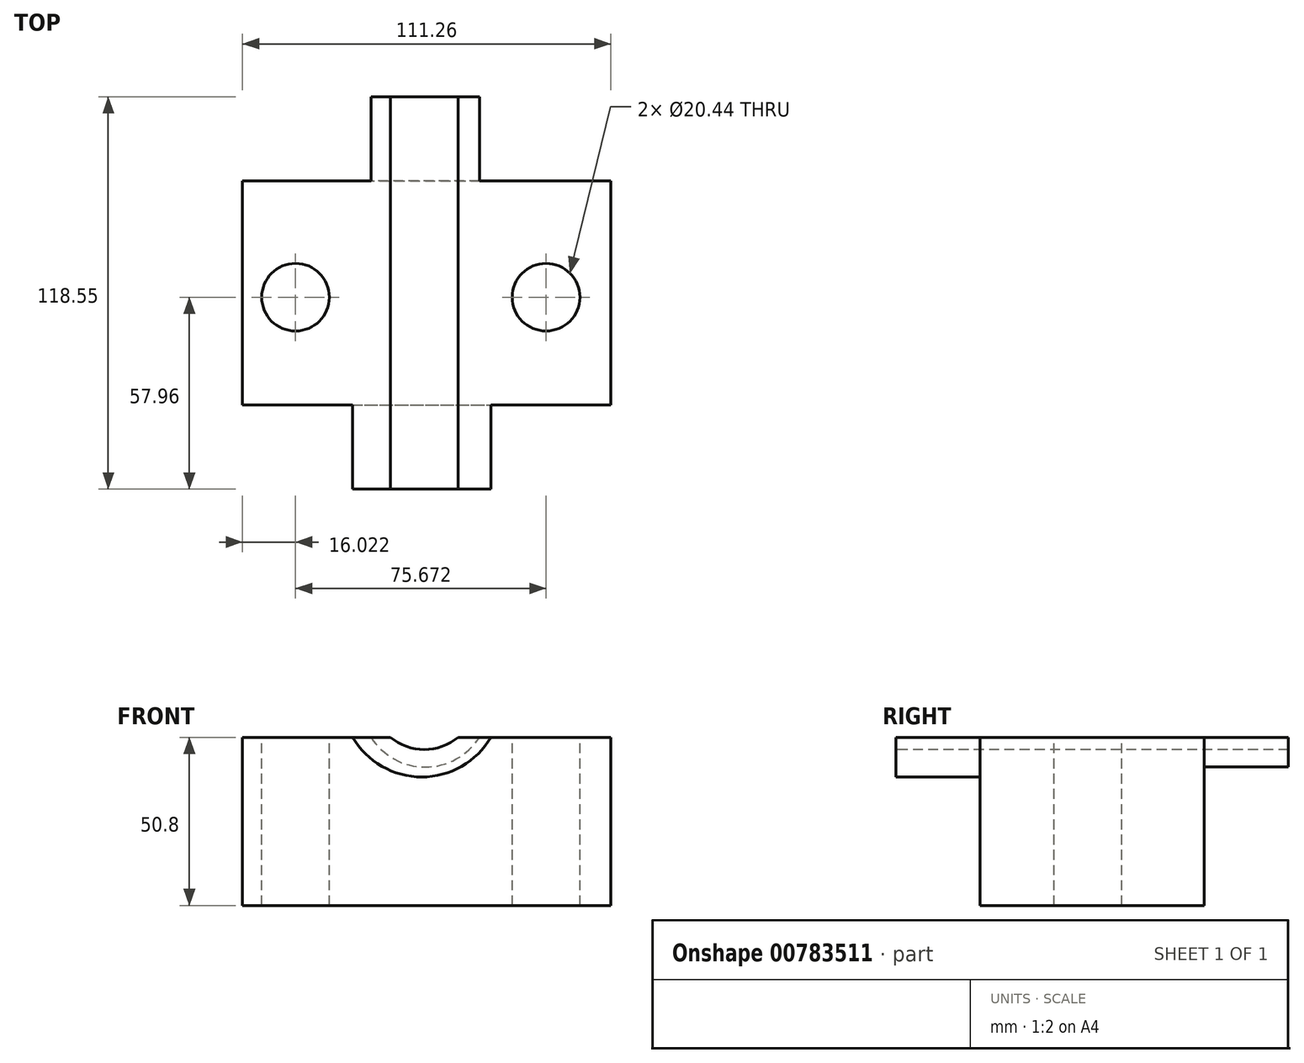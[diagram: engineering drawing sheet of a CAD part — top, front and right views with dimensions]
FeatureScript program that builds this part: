
annotation { "Feature Type Name" : "Feature", "Feature Type Description" : "" }
export const myFeature = defineFeature(function(context is Context, id is Id, definition is map)
    precondition{}
    {
        {
            var Q0;
            Q0=qCreatedBy(makeId("Top.planeOp"),FACE);
            var sketch = newSketch(context, id + "F0", { "sketchPlane" : qUnion([Q0])});
            skLineSegment(sketch, "E0.bottom", {"start": v(-54.46, -32.56) * mm, "end": v(56.8, -32.56) * mm});
            skLineSegment(sketch, "E0.top", {"start": v(-54.46, 35.19) * mm, "end": v(56.8, 35.19) * mm});
            skLineSegment(sketch, "E0.left", {"start": v(-54.46, -32.56) * mm, "end": v(-54.46, 35.19) * mm});
            skLineSegment(sketch, "E0.right", {"start": v(56.8, -32.56) * mm, "end": v(56.8, 35.19) * mm});
            skSolve(sketch);
        }
        {
            var Q0;
            Q0=makeQuery(id+"F0.imprint","IMPRINT",FACE,{"disambiguationData":[TD([[makeQuery(id+"F0.imprint","IMPRINT",EDGE,{"derivedFrom":sQuery(id+"F0.wireOp",EDGE,"E0.bottom")}),1.0]])]});
            extrude(context, id + "F1", {"entities" : qUnion([Q0]), "depth" : 50.8 * mm, "offsetDistance" : 25.4 * mm});
        }
        {
            var Q0;
            Q0=makeQuery(id+"F1.opExtrude","SWEPT_FACE",FACE,{"disambiguationData":[OSD([sQuery(id+"F0.wireOp",EDGE,"E0.bottom")])]});
            var sketch = newSketch(context, id + "F2", { "sketchPlane" : qUnion([Q0])});
            skArc(sketch, "E1", {"start": v(-9.78, 50.8) * mm, "mid": v(0.44, 47.12) * mm, "end": v(10.66, 50.8) * mm});
            skArc(sketch, "E2", {"start": v(-21.17, 50.8) * mm, "mid": v(-0.3, 38.81) * mm, "end": v(20.59, 50.8) * mm});
            skSolve(sketch);
        }
        {
            var Q0;
            {var subQ0=sQuery(id+"F2.wireOp",EDGE,"E1");Q0=makeQuery(id+"F2.imprint","IMPRINT",FACE,{"disambiguationData":[TD([[makeQuery(id+"F2.imprint","IMPRINT",EDGE,{"derivedFrom":subQ0}),1.0]])]});}
            extrude(context, id + "F3", {"entities" : qUnion([Q0]), "operationType" : NewBodyOperationType.REMOVE, "oppositeDirection" : true, "depth" : 127 * mm, "offsetDistance" : 25.4 * mm});
        }
        {
            var Q0;
            {var subQ0=sQuery(id+"F2.wireOp",EDGE,"E1");Q0=makeQuery(id+"F2.imprint","IMPRINT",FACE,{"disambiguationData":[TD([[makeQuery(id+"F2.imprint","IMPRINT",EDGE,{"derivedFrom":subQ0}),-1.0]])]});}
            extrude(context, id + "F4", {"entities" : qUnion([Q0]), "operationType" : NewBodyOperationType.ADD, "depth" : 25.4 * mm, "offsetDistance" : 25.4 * mm});
        }
        {
            var Q0;
            Q0=makeQuery(id+"F1.opExtrude","SWEPT_FACE",FACE,{"disambiguationData":[OSD([sQuery(id+"F0.wireOp",EDGE,"E0.top")])]});
            var sketch = newSketch(context, id + "F5", { "sketchPlane" : qUnion([Q0])});
            skArc(sketch, "E3", {"start": v(-17.1, 50.8) * mm, "mid": v(-0.73, 41.82) * mm, "end": v(15.64, 50.8) * mm});
            skSolve(sketch);
        }
        {
            var Q0;
            {var subQ0=sQuery(id+"F5.wireOp",EDGE,"E3");Q0=makeQuery(id+"F5.imprint","IMPRINT",FACE,{"disambiguationData":[TD([[makeQuery(id+"F5.imprint","IMPRINT",EDGE,{"derivedFrom":subQ0}),1.0]])]});}
            extrude(context, id + "F6", {"entities" : qUnion([Q0]), "operationType" : NewBodyOperationType.ADD, "depth" : 25.4 * mm, "offsetDistance" : 25.4 * mm});
        }
        {
            var Q0;
            {var subQ0=sQuery(id+"F0.wireOp",EDGE,"E0.right");var subQ1=sQuery(id+"F0.wireOp",EDGE,"E0.top");var subQ2=sQuery(id+"F0.wireOp",EDGE,"E0.bottom");var subQ3=makeQuery(id+"F1.opExtrude","CAP_FACE",FACE,{"disambiguationData":[OSD([subQ2,subQ1,sQuery(id+"F0.wireOp",EDGE,"E0.left"),subQ0])],"isStart":false});var subQ5=sQuery(id+"F2.wireOp",EDGE,"E1");var subQ7=makeQuery(id+"F1.opExtrude","SWEPT_FACE",FACE,{"disambiguationData":[OSD([subQ0])]});var subQ8=makeQuery(id+"F3.boolean.opBoolean","SPLIT",EDGE,{"disambiguationData":[TD([subQ7])],"derivedFrom":makeQuery(id+"F1.opExtrude","CAP_EDGE",EDGE,{"disambiguationData":[OSD([subQ1])],"isStart":false})});var subQ9=makeQuery(id+"F1.opExtrude","CAP_EDGE",EDGE,{"disambiguationData":[OSD([subQ2])],"isStart":false});Q0=makeQuery(id+"F6.boolean.opBoolean","MERGE",FACE,{"derivedFrom":[makeQuery(id+"F4.boolean.opBoolean","MERGE",FACE,{"derivedFrom":[makeQuery(id+"F3.boolean.opBoolean","SPLIT",FACE,{"disambiguationData":[TD([subQ7])],"derivedFrom":subQ3}),makeQuery(id+"F4.opExtrude","SWEPT_FACE",FACE,{"disambiguationData":[OSD([subQ2]),TDD([makeQuery(id+"F2.imprint","IMPRINT",EDGE,{"disambiguationData":[TD([[makeQuery(id+"F2.imprint","INTERSECT",VERTEX,{"disambiguationData":[OD(1.0)],"derivedFrom":[subQ9,subQ5]}),-1.0]])],"derivedFrom":subQ9})])]})]}),makeQuery(id+"F6.opExtrude","SWEPT_FACE",FACE,{"disambiguationData":[OSD([subQ1]),TDD([makeQuery(id+"F5.imprint","IMPRINT",EDGE,{"disambiguationData":[TD([[makeQuery(id+"F5.imprint","INTERSECT",VERTEX,{"derivedFrom":[subQ8,sQuery(id+"F5.wireOp",EDGE,"E3")]}),1.0]])],"derivedFrom":subQ8})])]})]});}
            var sketch = newSketch(context, id + "F7", { "sketchPlane" : qUnion([Q0])});
            skCircle(sketch, "E4", {"center": v(37.23, 0) * mm, "radius": 10.22 * mm});
            skCircle(sketch, "E5", {"center": v(-38.44, 0) * mm, "radius": 10.22 * mm});
            skSolve(sketch);
        }
        {
            var Q0;
            Q0=makeQuery(id+"F7.imprint","IMPRINT",FACE,{"disambiguationData":[TD([[makeQuery(id+"F7.imprint","IMPRINT",EDGE,{"derivedFrom":sQuery(id+"F7.wireOp",EDGE,"E5")}),1.0]])]});
            var Q1;
            Q1=makeQuery(id+"F7.imprint","IMPRINT",FACE,{"disambiguationData":[TD([[makeQuery(id+"F7.imprint","IMPRINT",EDGE,{"derivedFrom":sQuery(id+"F7.wireOp",EDGE,"E4")}),1.0]])]});
            extrude(context, id + "F8", {"entities" : qUnion([Q0, Q1]), "operationType" : NewBodyOperationType.REMOVE, "oppositeDirection" : true, "depth" : 127 * mm, "offsetDistance" : 25.4 * mm});
        }
    });
